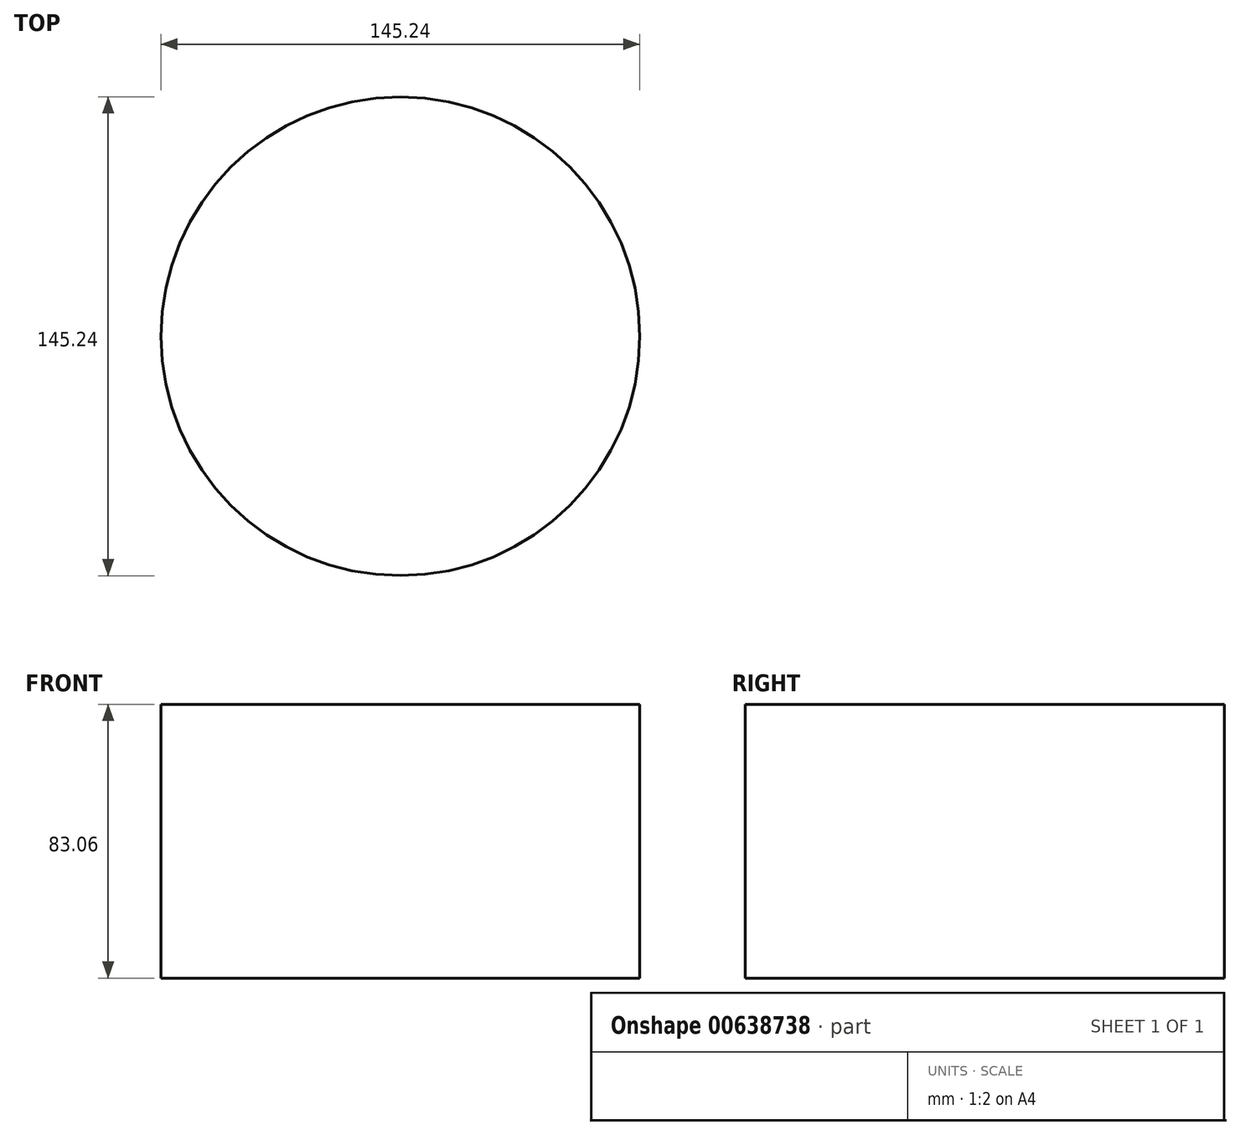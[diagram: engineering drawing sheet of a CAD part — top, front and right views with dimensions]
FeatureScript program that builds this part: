
annotation { "Feature Type Name" : "Feature", "Feature Type Description" : "" }
export const myFeature = defineFeature(function(context is Context, id is Id, definition is map)
    precondition{}
    {
        {
            var Q0;
            Q0=qCreatedBy(makeId("Top.planeOp"),FACE);
            var sketch = newSketch(context, id + "F0", { "sketchPlane" : qUnion([Q0])});
            skCircle(sketch, "E0", {"center": v(0, 0) * mm, "radius": 72.62 * mm});
            skSolve(sketch);
        }
        {
            var Q0;
            Q0=makeQuery(id+"F0.imprint","IMPRINT",FACE,{"disambiguationData":[TD([[makeQuery(id+"F0.imprint","IMPRINT",EDGE,{"derivedFrom":sQuery(id+"F0.wireOp",EDGE,"E0")}),1.0]])]});
            extrude(context, id + "F1", {"entities" : qUnion([Q0]), "depth" : 83.06 * mm, "offsetDistance" : 25.4 * mm});
        }
    });
